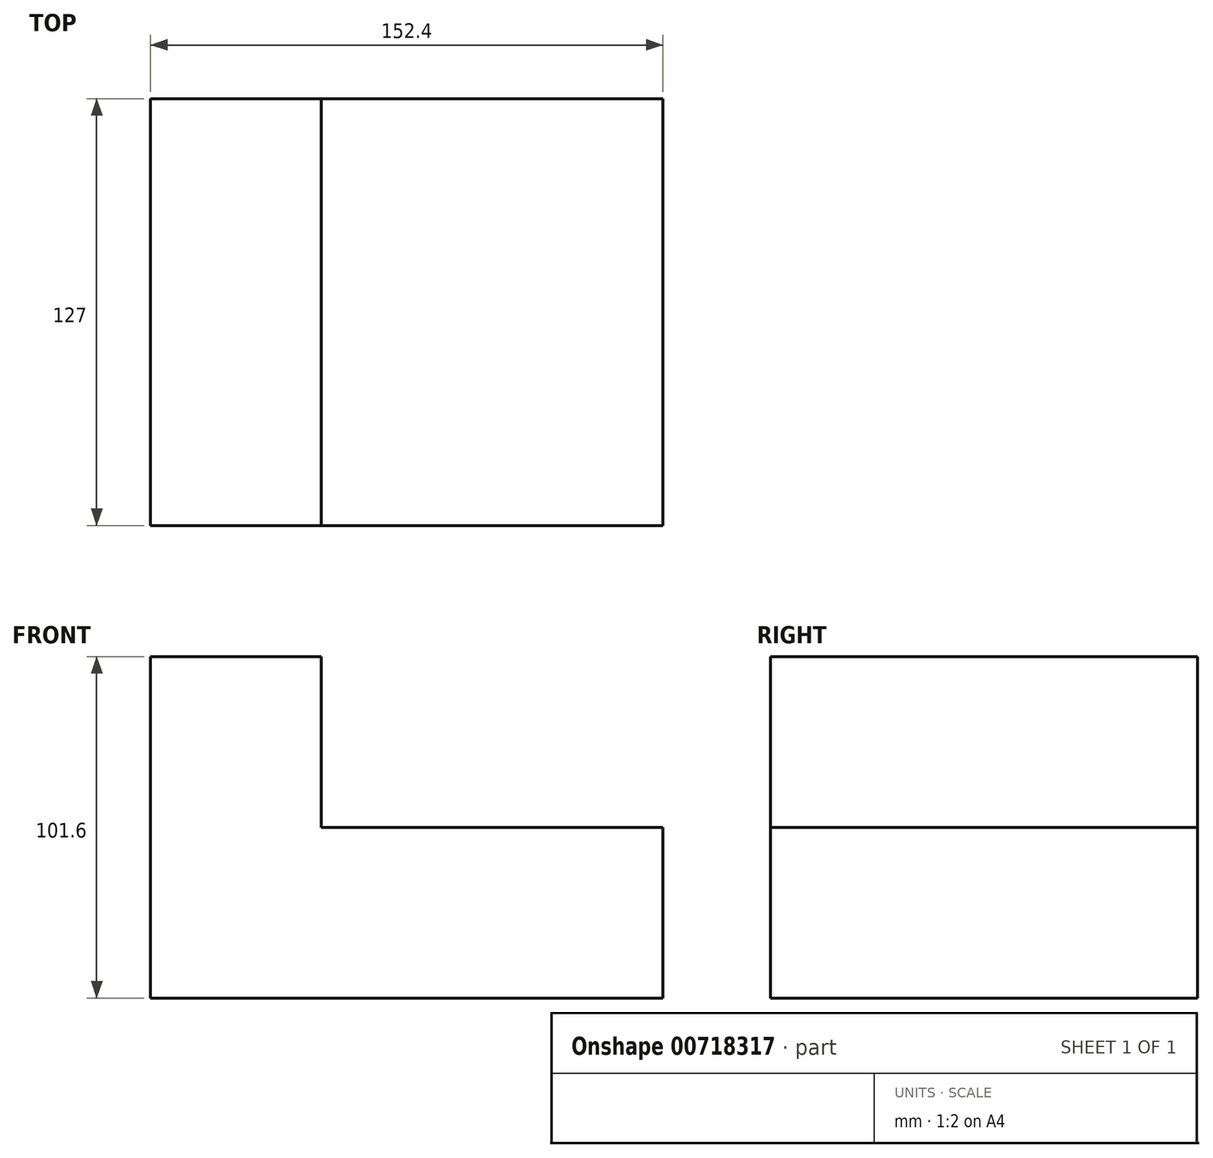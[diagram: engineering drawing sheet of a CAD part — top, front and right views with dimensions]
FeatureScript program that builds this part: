
annotation { "Feature Type Name" : "Feature", "Feature Type Description" : "" }
export const myFeature = defineFeature(function(context is Context, id is Id, definition is map)
    precondition{}
    {
        {
            var Q0;
            Q0=qCreatedBy(makeId("Front.planeOp"),FACE);
            var sketch = newSketch(context, id + "F0", { "sketchPlane" : qUnion([Q0])});
            skLineSegment(sketch, "E0", {"start": v(-45.24, -42.26) * mm, "end": v(107.16, -42.26) * mm});
            skLineSegment(sketch, "E1", {"start": v(107.16, 8.54) * mm, "end": v(107.16, -42.26) * mm});
            skLineSegment(sketch, "E2", {"start": v(5.56, 8.54) * mm, "end": v(107.16, 8.54) * mm});
            skLineSegment(sketch, "E3", {"start": v(5.56, 8.54) * mm, "end": v(5.56, 59.34) * mm});
            skLineSegment(sketch, "E4", {"start": v(5.56, 59.34) * mm, "end": v(-45.24, 59.34) * mm});
            skLineSegment(sketch, "E5", {"start": v(-45.24, 59.34) * mm, "end": v(-45.24, -42.26) * mm});
            skSolve(sketch);
        }
        {
            var Q0;
            Q0 = qSketchRegion(id + "F0", true);
            extrude(context, id + "F1", {"entities" : qUnion([Q0]), "depth" : 127 * mm, "offsetDistance" : 25.4 * mm});
        }
    });
